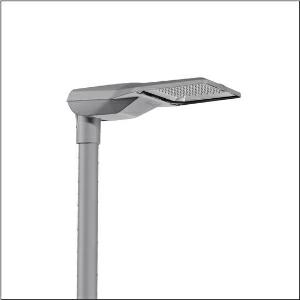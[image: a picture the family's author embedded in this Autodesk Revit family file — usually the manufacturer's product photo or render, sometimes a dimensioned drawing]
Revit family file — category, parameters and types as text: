
# Revit family: streetlight_sl_21_iq_midi___stw1_0a_5xe3e31d08nb_8d25
name_source: partatom
category: Lighting Fixtures
units: mm (PartAtom-declared; Revit-internal decimal feet)

## family parameters
Cut with Voids When Loaded = No
Host = Face
Light Source = No
Part Type = Normal
Room Calculation Point = No
Round Connector Dimension = Use Diameter
Shared = No

## types (1)
- --- (1 x LED, 23230 lm, 155.5 W, 3000K)
    Apparent Load = 155 VA
    CIE Flux Codes = 39 75 98 100 100
    Color Rendering = 70
    Color Temperature = 3000K
    Default Elevation = 1800 mm
    Description = Streetlight SL 21 iQ midi, mast luminaire, primary light control with lens, of PMMA, primary optical cover: cover, of toughened safety glass, transparent, light distribution: STW1.0a, light emission: direct distribution, primary light characteristic: asymmetric, installation type: post-top, side-entry, LED, High Power LED, rated luminous flux: 23.230lm, luminous efficacy: 149lm/W, light colour: 730, colour temperature: 3000K, control: Auto-Match, Temp-Guard, Lumen-Switch, Night-Set, Smart-Wire, Light-Fading, Desk-Remote (wireless, voltage-free reading and setting of iQ features in the workshop via application-optimized NFC function/RFID function), optimised constant luminous flux control (CLO 2.0), presetting dimming linear, mains connection: 230..240V, AC, 50/60Hz, start of lifetime: 156W, end of service life: 162W, reduction: 69W, luminaire housing, of diecast aluminium, powder-coated, Siteco® metallic grey (DB 702S), corrosivity category C5 mid according to DIN EN ISO 12944, please order mast flange separately, inclination adjustable: 0°, 5°, 10°, 15°, sealing non-destructively replaceable, multi-level sealing system, length: 644mm, width: 335mm, height: 110mm, mast flange for spigot size: 42mm (side-entry): 5XC10008XM4, 60/48mm (side-entry/post-top): 5XC10108XM2, 76/60mm (side-entry/post-top): 5XC10108XM1, protection rating (complete): IP66, insulation class (complete): insulation class II (safety insulation), certification: CE, ENEC, ENEC+, VDE, impact resistance: IK09, permissible operating ambient temperature for outdoor applications: -40..+50°C, standard-compliant lighting for roads and squares, packaging unit: 1 piece

Light Distribution: STW1.0a
    Height = 111 mm
    Lamp = 1 x LED
    Lamp Light Flux = 23230 lm
    Lamp Power = 155.5 W
    Lamp count = 1
    Length = 644 mm
    Luminous efficacy = 149 lm/W
    Manufacturer = Siteco
    ModVariant = No
    Model = 5XE3E31D08NB
    Number of Poles = 1
    OnlyDefault = Yes
    Power Factor = 1
    Product Name = Streetlight SL 21 iQ midi | STW1.0a
    Product group = mast luminaire | pylon top
    ProductGroupID = 6100
    Protection Class = Protection class II
    Protection Degree = IP 66
    RLX_Detail_Level = 1
    RLX_Emergency_Light_Flux = 0 lm
    RLX_Emergency_Type = 0
    RLX_Emergency_Type_DB = No
    RlxData = <blob elided: 91357 chars, md5=9fc215d9>
    Socket = socket
    Standby Power = 0 W
    System Light Flux = 23230 lm
    System Power = 155 W
    Type Comments = factory setting: luminous flux: 100 % | dim-lin: 254 | 823 mA
    Type Image = l_1004298.jpg
    URL = http://relux.com
    VarID = @adj_120357
    Voltage = 0 V
    Weight = 0.00 kg
    Width = 336 mm

## geometry (parser evidence)
native form markers: Blend x4, Sweep x13
no freeform markers — native parametric forms only
